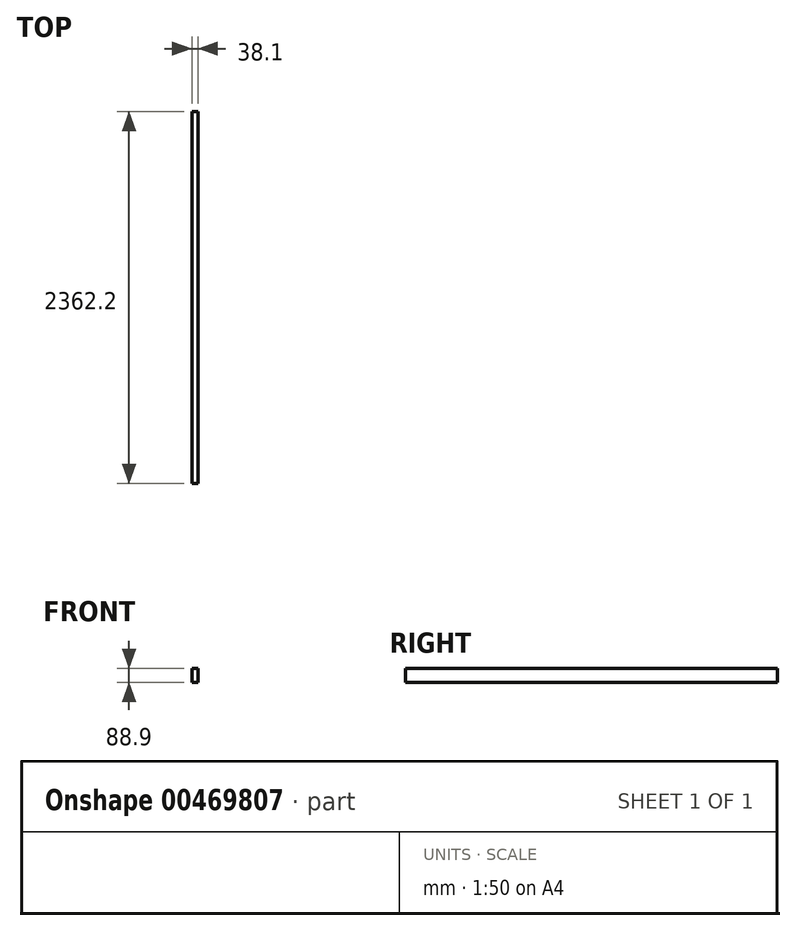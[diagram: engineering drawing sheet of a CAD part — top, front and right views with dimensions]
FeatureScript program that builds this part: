
annotation { "Feature Type Name" : "Feature", "Feature Type Description" : "" }
export const myFeature = defineFeature(function(context is Context, id is Id, definition is map)
    precondition{}
    {
        {
            var Q0;
            Q0=qCreatedBy(makeId("Front.planeOp"),FACE);
            var sketch = newSketch(context, id + "F0", { "sketchPlane" : qUnion([Q0])});
            skLineSegment(sketch, "E0.bottom", {"start": v(19.05, 44.45) * mm, "end": v(-19.05, 44.45) * mm});
            skLineSegment(sketch, "E0.top", {"start": v(19.05, -44.45) * mm, "end": v(-19.05, -44.45) * mm});
            skLineSegment(sketch, "E0.left", {"start": v(19.05, 44.45) * mm, "end": v(19.05, -44.45) * mm});
            skLineSegment(sketch, "E0.right", {"start": v(-19.05, 44.45) * mm, "end": v(-19.05, -44.45) * mm});
            skPoint(sketch, "E0.middle", {"position": v(0, 0) * mm});
            skSolve(sketch);
        }
        {
            var Q0;
            Q0=qSketchRegion(id+"F0",true);
            extrude(context, id + "F1", {"entities" : qUnion([Q0]), "oppositeDirection" : true, "depth" : 2362.2 * mm});
        }
    });
